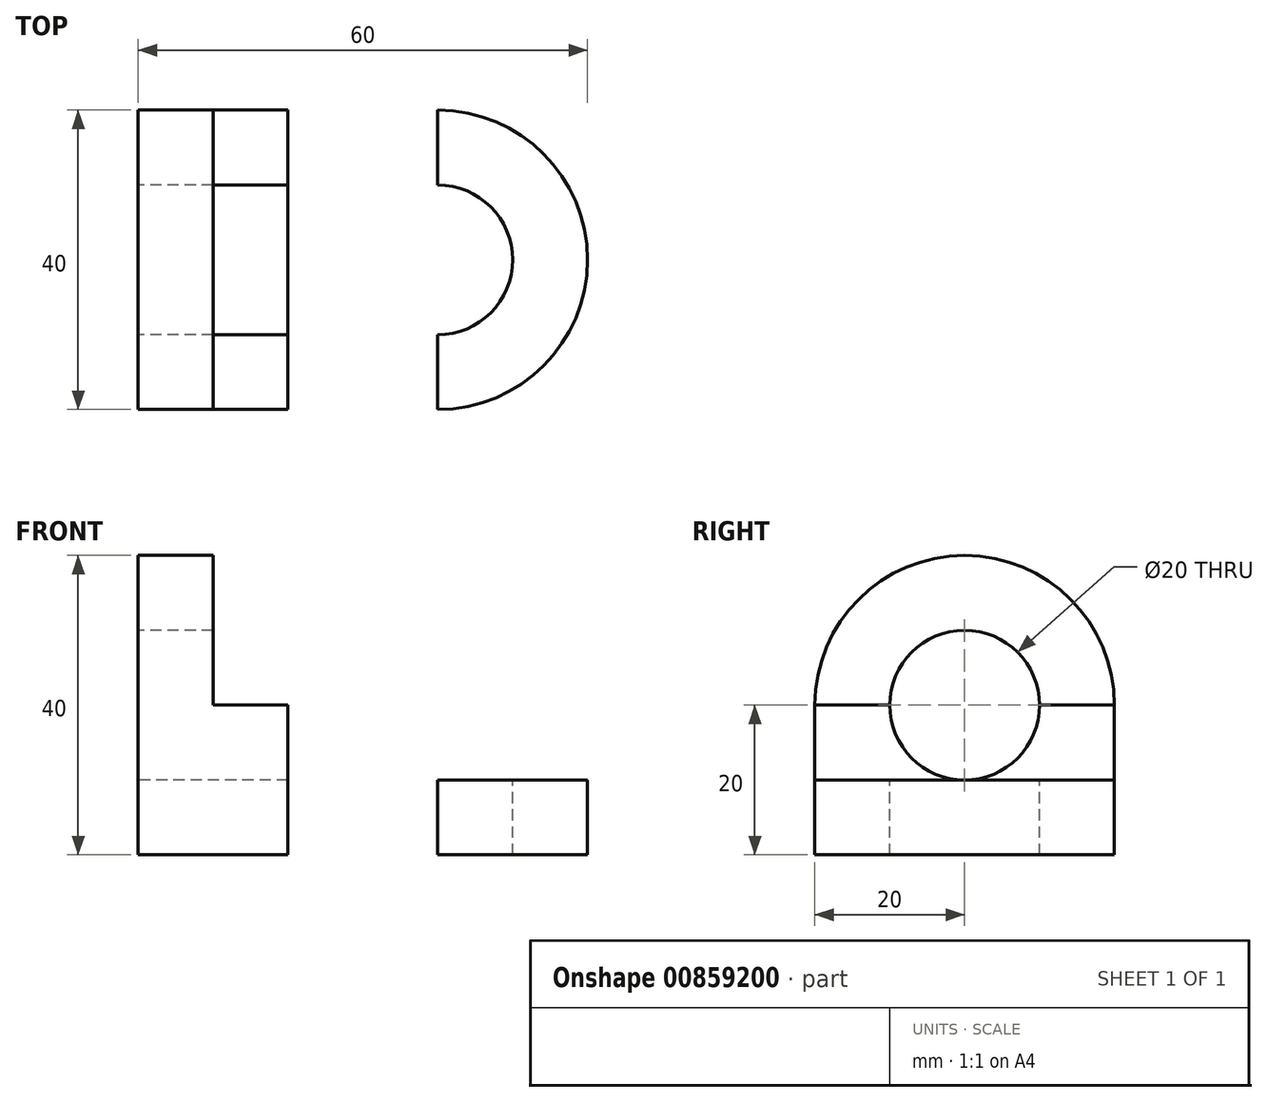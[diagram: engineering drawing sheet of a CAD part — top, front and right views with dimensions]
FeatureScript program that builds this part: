
annotation { "Feature Type Name" : "Feature", "Feature Type Description" : "" }
export const myFeature = defineFeature(function(context is Context, id is Id, definition is map)
    precondition{}
    {
        {
            var Q0;
            Q0=qCreatedBy(makeId("Top.planeOp"),FACE);
            var sketch = newSketch(context, id + "F0", { "sketchPlane" : qUnion([Q0])});
            skLineSegment(sketch, "E0.bottom", {"start": v(0, 0) * mm, "end": v(40, 0) * mm});
            skLineSegment(sketch, "E0.top", {"start": v(0, 40) * mm, "end": v(40, 40) * mm});
            skLineSegment(sketch, "E0.left", {"start": v(0, 0) * mm, "end": v(0, 40) * mm});
            skLineSegment(sketch, "E0.right", {"start": v(40, 0) * mm, "end": v(40, 40) * mm});
            skLineSegment(sketch, "E1", {"start": v(0, 20) * mm, "end": v(60.63, 20) * mm, "construction": true});
            skCircle(sketch, "E2", {"center": v(40, 20) * mm, "radius": 10 * mm});
            skArc(sketch, "E3", {"start": v(40, 0) * mm, "mid": v(60, 20) * mm, "end": v(40, 40) * mm});
            skLineSegment(sketch, "E4.bottom", {"start": v(0, 0) * mm, "end": v(20, 0) * mm});
            skLineSegment(sketch, "E4.top", {"start": v(0, 40) * mm, "end": v(20, 40) * mm});
            skLineSegment(sketch, "E4.right", {"start": v(20, 0) * mm, "end": v(20, 40) * mm});
            skLineSegment(sketch, "E5", {"start": v(10, 40) * mm, "end": v(10, 0) * mm});
            skSolve(sketch);
        }
        {
            var Q0;
            Q0=makeQuery(id+"F0.imprint","IMPRINT",FACE,{"disambiguationData":[TD([[makeQuery(id+"F0.imprint","IMPRINT",EDGE,{"derivedFrom":sQuery(id+"F0.wireOp",EDGE,"E4.bottom")}),1.0]])]});
            var Q1;
            {var subQ5=sQuery(id+"F0.wireOp",EDGE,"E0.bottom");Q1=makeQuery(id+"F0.imprint","IMPRINT",FACE,{"disambiguationData":[TD([[makeQuery(id+"F0.imprint","IMPRINT",EDGE,{"derivedFrom":subQ5}),1.0]])]});}
            var Q2;
            {var subQ0=sQuery(id+"F0.wireOp",EDGE,"E3");Q2=makeQuery(id+"F0.imprint","IMPRINT",FACE,{"disambiguationData":[TD([[makeQuery(id+"F0.imprint","IMPRINT",EDGE,{"derivedFrom":subQ0}),1.0]])]});}
            extrude(context, id + "F1", {"entities" : qUnion([Q0, Q1, Q2]), "oppositeDirection" : true, "depth" : 10 * mm, "offsetDistance" : 25 * mm});
        }
        {
            var Q0;
            {var subQ0=sQuery(id+"F0.wireOp",EDGE,"E4.right");Q0=makeQuery(id+"F0.imprint","IMPRINT",FACE,{"disambiguationData":[TD([[makeQuery(id+"F0.imprint","IMPRINT",EDGE,{"derivedFrom":subQ0}),1.0]])]});}
            extrude(context, id + "F2", {"entities" : qUnion([Q0]), "operationType" : NewBodyOperationType.ADD, "depth" : 10 * mm, "offsetDistance" : 25 * mm});
        }
        {
            var Q0;
            {var subQ0=sQuery(id+"F0.wireOp",EDGE,"E0.left");Q0=makeQuery(id+"F0.imprint","IMPRINT",FACE,{"disambiguationData":[TD([[makeQuery(id+"F0.imprint","IMPRINT",EDGE,{"derivedFrom":subQ0}),-1.0]])]});}
            extrude(context, id + "F3", {"entities" : qUnion([Q0]), "operationType" : NewBodyOperationType.ADD, "depth" : 20 * mm, "offsetDistance" : 25 * mm});
        }
        {
            var Q0;
            Q0=makeQuery(id+"F3.opExtrude","CAP_FACE",FACE,{"disambiguationData":[OSD([sQuery(id+"F0.wireOp",EDGE,"E4.bottom"),sQuery(id+"F0.wireOp",EDGE,"E4.top"),sQuery(id+"F0.wireOp",EDGE,"E0.left"),sQuery(id+"F0.wireOp",EDGE,"E5")])],"isStart":false});
            extrude(context, id + "F4", {"entities" : qUnion([Q0]), "operationType" : NewBodyOperationType.ADD, "depth" : 10 * mm, "offsetDistance" : 25 * mm});
        }
        {
            var Q0;
            {var subQ0=sQuery(id+"F0.wireOp",EDGE,"E0.left");Q0=makeQuery(id+"F3.boolean.opBoolean","MERGE",FACE,{"derivedFrom":[makeQuery(id+"F1.opExtrude","SWEPT_FACE",FACE,{"disambiguationData":[OSD([subQ0])]}),makeQuery(id+"F3.opExtrude","SWEPT_FACE",FACE,{"disambiguationData":[OSD([subQ0])]})]});}
            var sketch = newSketch(context, id + "F5", { "sketchPlane" : qUnion([Q0])});
            skCircle(sketch, "E6", {"center": v(-20, 10) * mm, "radius": 10 * mm});
            skPoint(sketch, "E6.centerSnap0", {"position": v(-20, 20) * mm});
            skArc(sketch, "E7", {"start": v(0, 10) * mm, "mid": v(-20, 30) * mm, "end": v(-40, 10) * mm});
            skLineSegment(sketch, "E8", {"start": v(0, 10) * mm, "end": v(-40, 10) * mm});
            skLineSegment(sketch, "E9", {"start": v(-20, 30) * mm, "end": v(-40, 30) * mm});
            skLineSegment(sketch, "E10", {"start": v(-40, 30) * mm, "end": v(-40, 10.33) * mm});
            skLineSegment(sketch, "E11", {"start": v(0, 10) * mm, "end": v(0, 30) * mm});
            skLineSegment(sketch, "E12", {"start": v(0, 30) * mm, "end": v(-20, 30) * mm});
            skSolve(sketch);
        }
        {
            var Q0;
            {var subQ5=sQuery(id+"F5.wireOp",EDGE,"E9");Q0=makeQuery(id+"F5.imprint","IMPRINT",FACE,{"disambiguationData":[TD([[makeQuery(id+"F5.imprint","IMPRINT",EDGE,{"derivedFrom":subQ5}),1.0]])]});}
            var Q1;
            {var subQ0=sQuery(id+"F5.wireOp",EDGE,"E11");Q1=makeQuery(id+"F5.imprint","IMPRINT",FACE,{"disambiguationData":[TD([[makeQuery(id+"F5.imprint","IMPRINT",EDGE,{"derivedFrom":subQ0}),1.0]])]});}
            extrude(context, id + "F6", {"entities" : qUnion([Q0, Q1]), "operationType" : NewBodyOperationType.REMOVE, "oppositeDirection" : true, "depth" : 10 * mm, "offsetDistance" : 25 * mm});
        }
        {
            var Q0;
            {var subQ0=sQuery(id+"F5.wireOp",EDGE,"E8");var subQ1=sQuery(id+"F5.wireOp",EDGE,"E6");var subQ2=makeQuery(id+"F5.imprint","INTERSECT",VERTEX,{"disambiguationData":[OD(0.0)],"derivedFrom":[subQ1,subQ0]});Q0=makeQuery(id+"F5.imprint","IMPRINT",FACE,{"disambiguationData":[TD([[makeQuery(id+"F5.imprint","IMPRINT",EDGE,{"disambiguationData":[TD([[subQ2,1.0]])],"derivedFrom":subQ1}),1.0]])]});}
            var Q1;
            {var subQ0=sQuery(id+"F5.wireOp",EDGE,"E8");var subQ1=sQuery(id+"F5.wireOp",EDGE,"E6");var subQ2=makeQuery(id+"F5.imprint","INTERSECT",VERTEX,{"disambiguationData":[OD(0.0)],"derivedFrom":[subQ1,subQ0]});Q1=makeQuery(id+"F5.imprint","IMPRINT",FACE,{"disambiguationData":[TD([[makeQuery(id+"F5.imprint","IMPRINT",EDGE,{"disambiguationData":[TD([[subQ2,-1.0]])],"derivedFrom":subQ1}),1.0]])]});}
            extrude(context, id + "F7", {"entities" : qUnion([Q0, Q1]), "operationType" : NewBodyOperationType.REMOVE, "oppositeDirection" : true, "depth" : 20 * mm, "offsetDistance" : 25 * mm});
        }
    });
